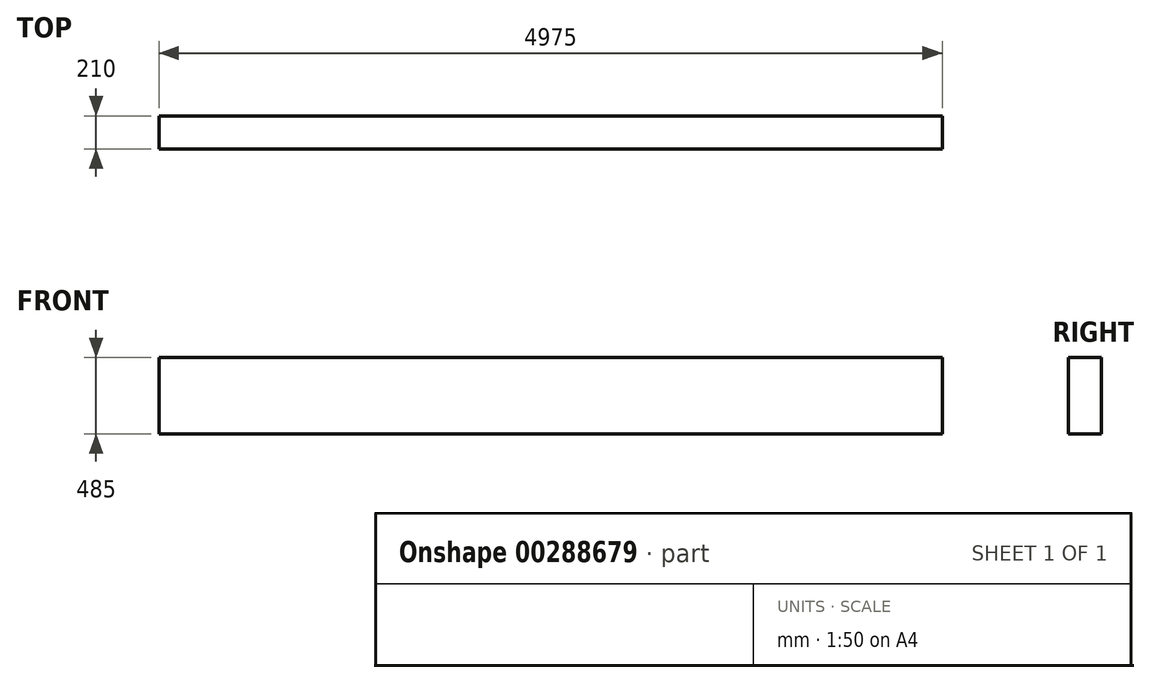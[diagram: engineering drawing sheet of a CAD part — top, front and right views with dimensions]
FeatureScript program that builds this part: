
annotation { "Feature Type Name" : "Feature", "Feature Type Description" : "" }
export const myFeature = defineFeature(function(context is Context, id is Id, definition is map)
    precondition{}
    {
        {
            var Q0;
            Q0=qCreatedBy(makeId("Top.planeOp"),FACE);
            var sketch = newSketch(context, id + "F0", { "sketchPlane" : qUnion([Q0])});
            skLineSegment(sketch, "E0.bottom", {"start": v(0, 0) * mm, "end": v(-4975, 0) * mm});
            skLineSegment(sketch, "E0.top", {"start": v(0, 210) * mm, "end": v(-4975, 210) * mm});
            skLineSegment(sketch, "E0.left", {"start": v(0, 0) * mm, "end": v(0, 210) * mm});
            skLineSegment(sketch, "E0.right", {"start": v(-4975, 0) * mm, "end": v(-4975, 210) * mm});
            skSolve(sketch);
        }
        {
            var Q0;
            Q0 = qSketchRegion(id + "F0", true);
            extrude(context, id + "F1", {"entities" : qUnion([Q0]), "depth" : (325 + 160) * mm});
        }
    });
